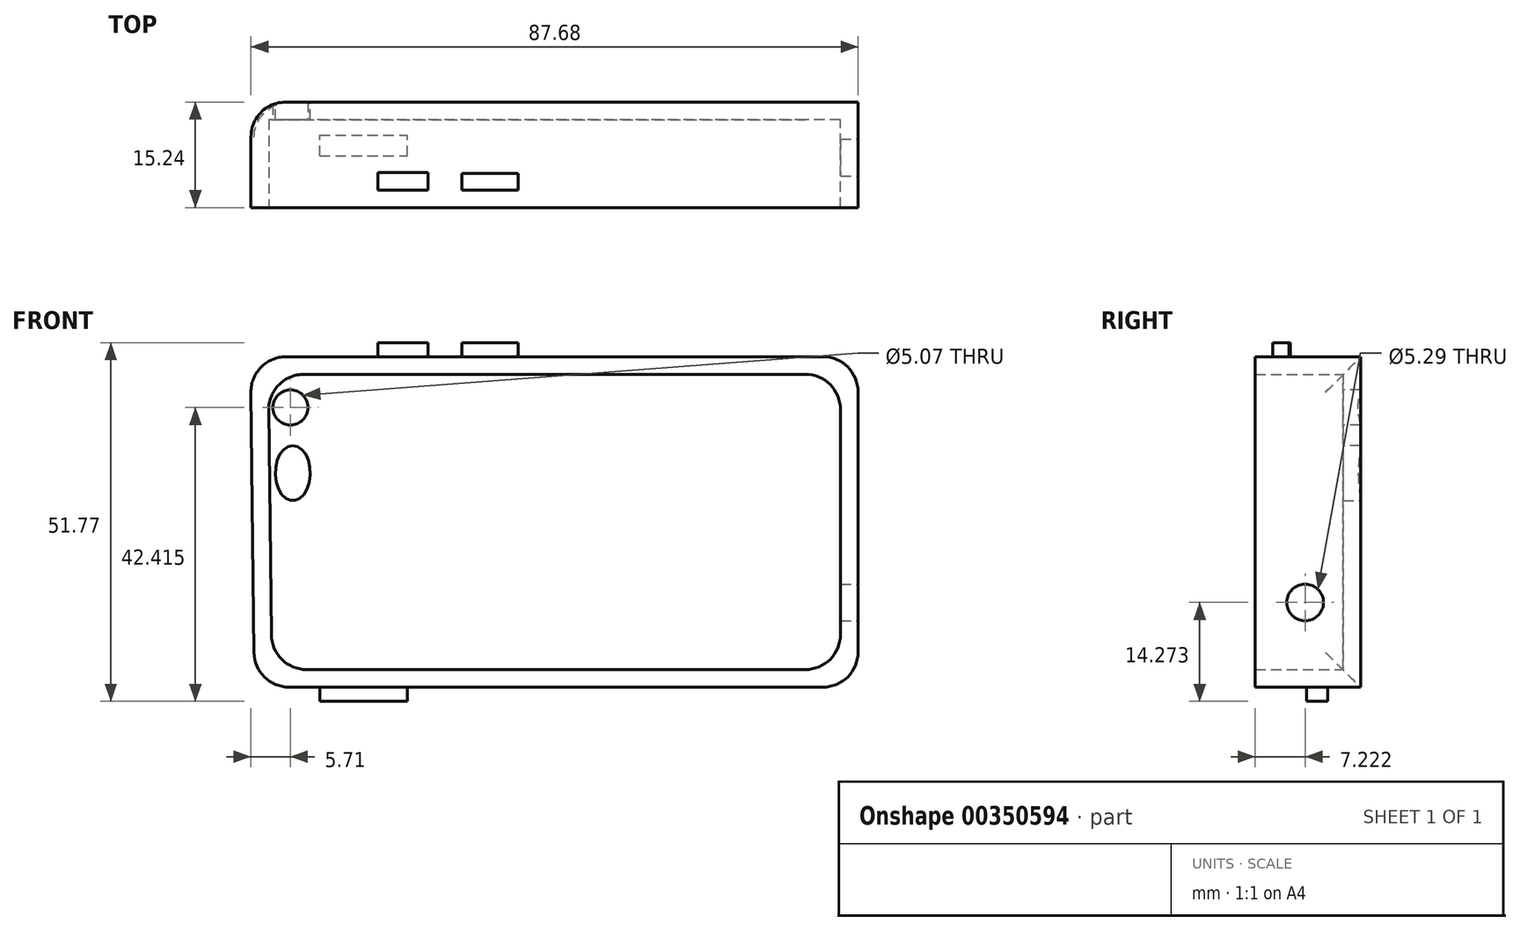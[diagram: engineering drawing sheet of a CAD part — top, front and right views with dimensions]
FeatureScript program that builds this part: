
annotation { "Feature Type Name" : "Feature", "Feature Type Description" : "" }
export const myFeature = defineFeature(function(context is Context, id is Id, definition is map)
    precondition{}
    {
        {
            var Q0;
            Q0=qCreatedBy(makeId("Front.planeOp"),FACE);
            var sketch = newSketch(context, id + "F0", { "sketchPlane" : qUnion([Q0])});
            skLineSegment(sketch, "E0", {"start": v(-50.54, 37.34) * mm, "end": v(37.2, 37.34) * mm});
            skLineSegment(sketch, "E1", {"start": v(37.2, 37.34) * mm, "end": v(37.2, -10.36) * mm});
            skLineSegment(sketch, "E2", {"start": v(37.2, -10.36) * mm, "end": v(-49.97, -10.36) * mm});
            skLineSegment(sketch, "E3", {"start": v(-49.97, -10.36) * mm, "end": v(-50.54, 37.34) * mm});
            skSolve(sketch);
        }
        {
            var Q0;
            Q0=makeQuery(id+"F0.imprint","IMPRINT",FACE,{"disambiguationData":[TD([[makeQuery(id+"F0.imprint","IMPRINT",EDGE,{"derivedFrom":sQuery(id+"F0.wireOp",EDGE,"E0")}),-1.0]])]});
            extrude(context, id + "F1", {"entities" : qUnion([Q0]), "endBound" : BoundingType.SYMMETRIC, "depth" : 25.4 * mm});
        }
        {
            var Q0;
            Q0=makeQuery(id+"F1.opExtrude","CAP_FACE",FACE,{"disambiguationData":[OSD([sQuery(id+"F0.wireOp",EDGE,"E0"),sQuery(id+"F0.wireOp",EDGE,"E1"),sQuery(id+"F0.wireOp",EDGE,"E2"),sQuery(id+"F0.wireOp",EDGE,"E3")])],"isStart":false});
            shell(context, id + "F2", {"entities" : qUnion([Q0]), "thickness" : 2.54 * mm});
        }
        {
            var Q0;
            Q0=makeQuery(id+"F2.opShell","OFFSET_FACE",FACE,{"disambiguationData":[OSD([sQuery(id+"F0.wireOp",EDGE,"E0"),sQuery(id+"F0.wireOp",EDGE,"E1"),sQuery(id+"F0.wireOp",EDGE,"E2"),sQuery(id+"F0.wireOp",EDGE,"E3")])]});
            var sketch = newSketch(context, id + "F3", { "sketchPlane" : qUnion([Q0])});
            skCircle(sketch, "E4", {"center": v(-44.77, 30.01) * mm, "radius": 2.53 * mm});
            skSolve(sketch);
        }
        {
            var Q0;
            Q0=makeQuery(id+"F3.imprint","IMPRINT",FACE,{"disambiguationData":[TD([[makeQuery(id+"F3.imprint","IMPRINT",EDGE,{"derivedFrom":sQuery(id+"F3.wireOp",EDGE,"E4")}),1.0]])]});
            extrude(context, id + "F4", {"entities" : qUnion([Q0]), "operationType" : NewBodyOperationType.REMOVE, "oppositeDirection" : true, "depth" : 25.4 * mm});
        }
        {
            var Q0;
            Q0=makeQuery(id+"F1.opExtrude","SWEPT_FACE",FACE,{"disambiguationData":[OSD([sQuery(id+"F0.wireOp",EDGE,"E2")])]});
            var sketch = newSketch(context, id + "F5", { "sketchPlane" : qUnion([Q0])});
            skLineSegment(sketch, "E5.bottom", {"start": v(-40.56, -4.92) * mm, "end": v(-27.9, -4.92) * mm});
            skLineSegment(sketch, "E5.top", {"start": v(-40.56, -7.93) * mm, "end": v(-27.9, -7.93) * mm});
            skLineSegment(sketch, "E5.left", {"start": v(-40.56, -4.92) * mm, "end": v(-40.56, -7.93) * mm});
            skLineSegment(sketch, "E5.right", {"start": v(-27.9, -4.92) * mm, "end": v(-27.9, -7.93) * mm});
            skSolve(sketch);
        }
        {
            var Q0;
            Q0=makeQuery(id+"F5.imprint","IMPRINT",FACE,{"disambiguationData":[TD([[makeQuery(id+"F5.imprint","IMPRINT",EDGE,{"derivedFrom":sQuery(id+"F5.wireOp",EDGE,"E5.bottom")}),-1.0]])]});
            extrude(context, id + "F6", {"entities" : qUnion([Q0]), "operationType" : NewBodyOperationType.ADD, "depth" : 2.03 * mm});
        }
        {
            var Q0;
            Q0=makeQuery(id+"F1.opExtrude","SWEPT_EDGE",EDGE,{"disambiguationData":[OSD([sQuery(id+"F0.wireOp",EDGE,"E0"),sQuery(id+"F0.wireOp",EDGE,"E3")])]});
            var Q1;
            Q1=makeQuery(id+"F1.opExtrude","CAP_EDGE",EDGE,{"disambiguationData":[OSD([sQuery(id+"F0.wireOp",EDGE,"E3")])],"isStart":true});
            var Q2;
            Q2=makeQuery(id+"F1.opExtrude","SWEPT_EDGE",EDGE,{"disambiguationData":[OSD([sQuery(id+"F0.wireOp",EDGE,"E2"),sQuery(id+"F0.wireOp",EDGE,"E3")])]});
            var Q3;
            Q3=makeQuery(id+"F1.opExtrude","SWEPT_EDGE",EDGE,{"disambiguationData":[OSD([sQuery(id+"F0.wireOp",EDGE,"E1"),sQuery(id+"F0.wireOp",EDGE,"E2")])]});
            var Q4;
            Q4=makeQuery(id+"F1.opExtrude","SWEPT_EDGE",EDGE,{"disambiguationData":[OSD([sQuery(id+"F0.wireOp",EDGE,"E0"),sQuery(id+"F0.wireOp",EDGE,"E1")])]});
            fillet(context, id + "F7", {"entities" : qUnion([Q0, Q1, Q2, Q3, Q4]), "radius" : 5.08 * mm, "tangentPropagation" : true, "allowEdgeOverflow" : false});
        }
        {
            var Q0;
            Q0=makeQuery(id+"F1.opExtrude","SWEPT_FACE",FACE,{"disambiguationData":[OSD([sQuery(id+"F0.wireOp",EDGE,"E0")])]});
            var sketch = newSketch(context, id + "F8", { "sketchPlane" : qUnion([Q0])});
            skLineSegment(sketch, "E6.bottom", {"start": v(-32.15, 0) * mm, "end": v(-24.89, 0) * mm});
            skLineSegment(sketch, "E6.top", {"start": v(-32.15, 2.55) * mm, "end": v(-24.89, 2.55) * mm});
            skLineSegment(sketch, "E6.left", {"start": v(-32.15, 0) * mm, "end": v(-32.15, 2.55) * mm});
            skLineSegment(sketch, "E6.right", {"start": v(-24.89, 0) * mm, "end": v(-24.89, 2.55) * mm});
            skLineSegment(sketch, "E7.bottom", {"start": v(-19.99, 0) * mm, "end": v(-11.89, 0) * mm});
            skLineSegment(sketch, "E7.top", {"start": v(-19.99, 2.38) * mm, "end": v(-11.89, 2.38) * mm});
            skLineSegment(sketch, "E7.left", {"start": v(-19.99, 0) * mm, "end": v(-19.99, 2.38) * mm});
            skLineSegment(sketch, "E7.right", {"start": v(-11.89, 0) * mm, "end": v(-11.89, 2.38) * mm});
            skSolve(sketch);
        }
        {
            var Q0;
            Q0 = qSketchRegion(id + "F8", true);
            extrude(context, id + "F9", {"entities" : qUnion([Q0]), "operationType" : NewBodyOperationType.ADD, "depth" : 2.03 * mm});
        }
        {
            var Q0;
            Q0=makeQuery(id+"F2.opShell","OFFSET_FACE",FACE,{"disambiguationData":[OSD([sQuery(id+"F0.wireOp",EDGE,"E0"),sQuery(id+"F0.wireOp",EDGE,"E1"),sQuery(id+"F0.wireOp",EDGE,"E2"),sQuery(id+"F0.wireOp",EDGE,"E3")])]});
            var sketch = newSketch(context, id + "F10", { "sketchPlane" : qUnion([Q0])});
            skEllipse(sketch, "E8", {"center": v(-44.43, 20.55) * mm, "majorRadius": 3.98 * mm, "minorRadius": 2.52 * mm, "majorAxis": v(0, 1)});
            skSolve(sketch);
        }
        {
            var Q0;
            Q0=makeQuery(id+"F10.imprint","IMPRINT",FACE,{"disambiguationData":[TD([[makeQuery(id+"F10.imprint","IMPRINT",EDGE,{"derivedFrom":sQuery(id+"F10.wireOp",EDGE,"E8")}),1.0]])]});
            extrude(context, id + "F11", {"entities" : qUnion([Q0]), "operationType" : NewBodyOperationType.REMOVE, "oppositeDirection" : true, "depth" : 5.33 * mm});
        }
        {
            var Q0;
            Q0=makeQuery(id+"F1.opExtrude","CAP_FACE",FACE,{"disambiguationData":[OSD([sQuery(id+"F0.wireOp",EDGE,"E0"),sQuery(id+"F0.wireOp",EDGE,"E1"),sQuery(id+"F0.wireOp",EDGE,"E2"),sQuery(id+"F0.wireOp",EDGE,"E3")])],"isStart":false});
            extrude(context, id + "F12", {"entities" : qUnion([Q0]), "operationType" : NewBodyOperationType.REMOVE, "oppositeDirection" : true, "depth" : 10.16 * mm});
        }
        {
            var Q0;
            Q0=makeQuery(id+"F2.opShell","OFFSET_EDGE",EDGE,{"disambiguationData":[OSD([sQuery(id+"F0.wireOp",EDGE,"E2"),sQuery(id+"F0.wireOp",EDGE,"E3")])]});
            var Q1;
            Q1=makeQuery(id+"F2.opShell","OFFSET_EDGE",EDGE,{"disambiguationData":[OSD([sQuery(id+"F0.wireOp",EDGE,"E0"),sQuery(id+"F0.wireOp",EDGE,"E3")])]});
            var Q2;
            Q2=makeQuery(id+"F2.opShell","OFFSET_EDGE",EDGE,{"disambiguationData":[OSD([sQuery(id+"F0.wireOp",EDGE,"E1"),sQuery(id+"F0.wireOp",EDGE,"E2")])]});
            var Q3;
            Q3=makeQuery(id+"F2.opShell","OFFSET_EDGE",EDGE,{"disambiguationData":[OSD([sQuery(id+"F0.wireOp",EDGE,"E0"),sQuery(id+"F0.wireOp",EDGE,"E1")])]});
            fillet(context, id + "F13", {"entities" : qUnion([Q0, Q1, Q2, Q3]), "radius" : 5.08 * mm, "tangentPropagation" : true, "allowEdgeOverflow" : false});
        }
        {
            var Q0;
            Q0=makeQuery(id+"F1.opExtrude","SWEPT_FACE",FACE,{"disambiguationData":[OSD([sQuery(id+"F0.wireOp",EDGE,"E1")])]});
            var sketch = newSketch(context, id + "F14", { "sketchPlane" : qUnion([Q0])});
            skCircle(sketch, "E9", {"center": v(4.68, 1.87) * mm, "radius": 2.64 * mm});
            skSolve(sketch);
        }
        {
            var Q0;
            Q0=makeQuery(id+"F14.imprint","IMPRINT",FACE,{"disambiguationData":[TD([[makeQuery(id+"F14.imprint","IMPRINT",EDGE,{"derivedFrom":sQuery(id+"F14.wireOp",EDGE,"E9")}),1.0]])]});
            extrude(context, id + "F15", {"entities" : qUnion([Q0]), "operationType" : NewBodyOperationType.REMOVE, "oppositeDirection" : true, "depth" : 25.4 * mm});
        }
    });
